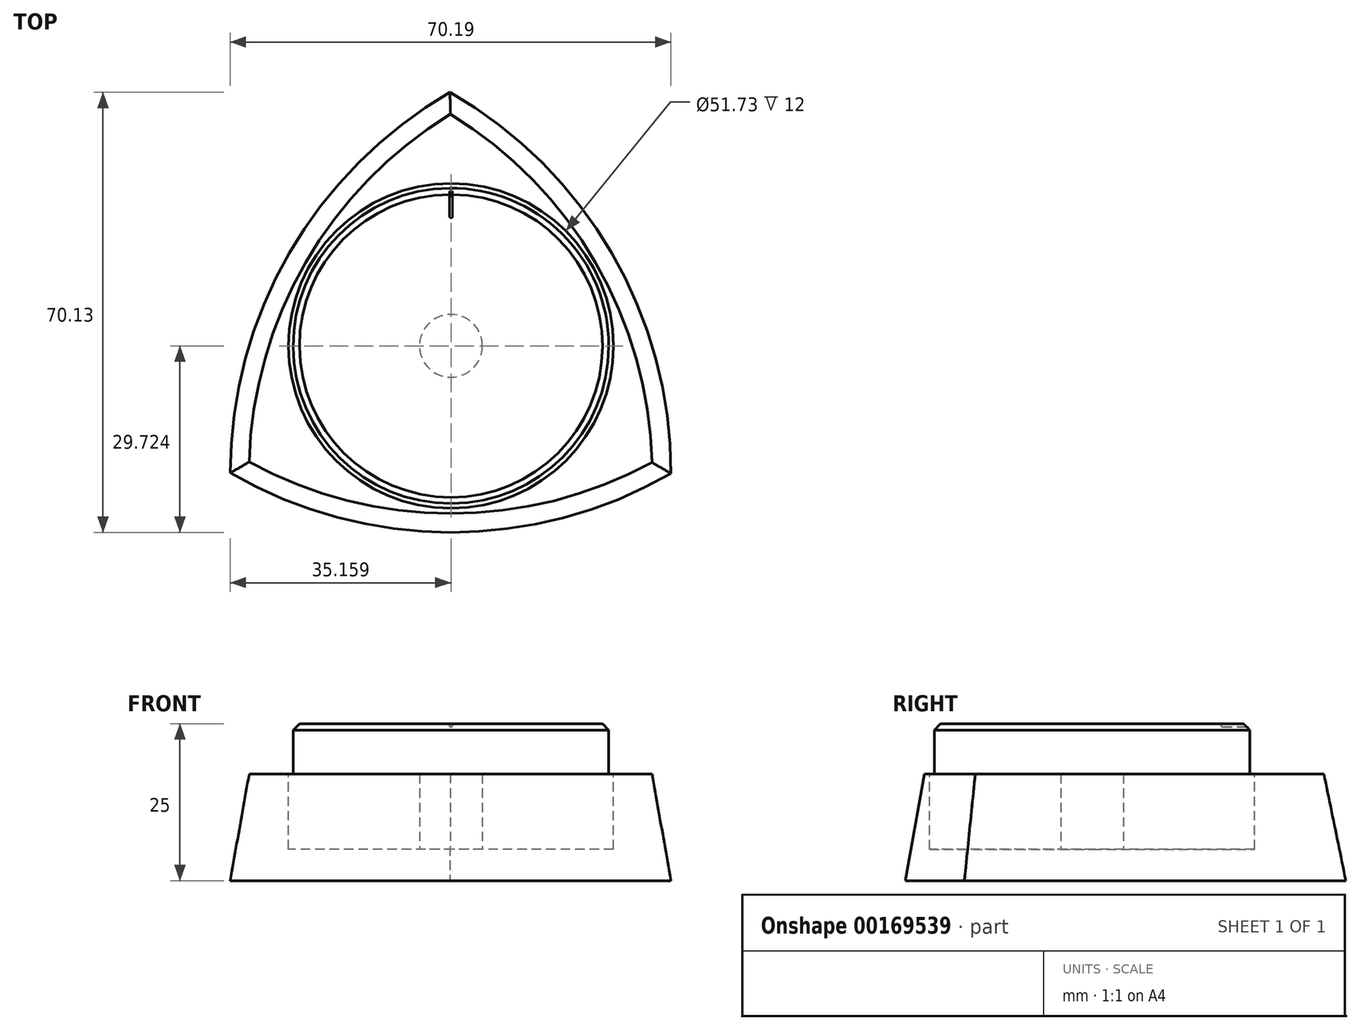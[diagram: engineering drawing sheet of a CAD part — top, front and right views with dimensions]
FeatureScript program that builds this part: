
annotation { "Feature Type Name" : "Feature", "Feature Type Description" : "" }
export const myFeature = defineFeature(function(context is Context, id is Id, definition is map)
    precondition{}
    {
        {
            var Q0;
            Q0=qCreatedBy(makeId("Top.planeOp"),FACE);
            var sketch = newSketch(context, id + "F0", { "sketchPlane" : qUnion([Q0])});
            skLineSegment(sketch, "E0", {"start": v(-35, 0) * mm, "end": v(35, 0) * mm});
            skLineSegment(sketch, "E1", {"start": v(35, 0) * mm, "end": v(0, 60.62) * mm});
            skLineSegment(sketch, "E2", {"start": v(0, 60.62) * mm, "end": v(-35, 0) * mm});
            skArc(sketch, "E3", {"start": v(35.02, -0.01) * mm, "mid": v(25.6, 35.08) * mm, "end": v(-0.15, 60.73) * mm});
            skArc(sketch, "E4", {"start": v(-0.15, 60.73) * mm, "mid": v(-25.77, 35.08) * mm, "end": v(-35.17, 0.07) * mm});
            skArc(sketch, "E5", {"start": v(-35.17, 0.07) * mm, "mid": v(-0.08, -9.4) * mm, "end": v(35.02, -0.01) * mm});
            skSolve(sketch);
        }
        {
            var Q0;
            Q0=makeQuery(id+"F0.imprint","IMPRINT",FACE,{"disambiguationData":[TD([[makeQuery(id+"F0.imprint","IMPRINT",EDGE,{"derivedFrom":sQuery(id+"F0.wireOp",EDGE,"E0")}),1.0]])]});
            var Q1;
            Q1=makeQuery(id+"F0.imprint","IMPRINT",FACE,{"disambiguationData":[TD([[makeQuery(id+"F0.imprint","IMPRINT",EDGE,{"derivedFrom":sQuery(id+"F0.wireOp",EDGE,"E0")}),-1.0]])]});
            extrude(context, id + "F1", {"entities" : qUnion([Q0, Q1]), "depth" : 17 * mm, "hasDraft" : true, "draftAngle" : 10 * degree, "draftPullDirection" : true});
        }
        {
            var Q0;
            Q0=makeQuery(id+"F1.opExtrude","CAP_FACE",FACE,{"disambiguationData":[OSD([sQuery(id+"F0.wireOp",EDGE,"E3"),sQuery(id+"F0.wireOp",EDGE,"E4"),sQuery(id+"F0.wireOp",EDGE,"E5")])],"isStart":false});
            var sketch = newSketch(context, id + "F2", { "sketchPlane" : qUnion([Q0])});
            skLineSegment(sketch, "E6", {"start": v(0.08, -6.4) * mm, "end": v(-0.14, 57.24) * mm, "construction": true});
            skPoint(sketch, "E6.startSnap0", {"position": v(-0.08, -6.4) * mm});
            skLineSegment(sketch, "E7", {"start": v(-23.17, 33.59) * mm, "end": v(32, 1.73) * mm, "construction": true});
            skLineSegment(sketch, "E8", {"start": v(23, 33.58) * mm, "end": v(-32.14, 1.81) * mm, "construction": true});
            skCircle(sketch, "E9", {"center": v(-0.01, 20.32) * mm, "radius": 25.87 * mm});
            skSolve(sketch);
        }
        {
            var Q0;
            Q0=makeQuery(id+"F2.imprint","IMPRINT",FACE,{"disambiguationData":[TD([[makeQuery(id+"F2.imprint","IMPRINT",EDGE,{"derivedFrom":sQuery(id+"F2.wireOp",EDGE,"E9")}),1.0]])]});
            extrude(context, id + "F3", {"entities" : qUnion([Q0]), "operationType" : NewBodyOperationType.REMOVE, "oppositeDirection" : true, "depth" : 12 * mm});
        }
        {
            var Q0;
            Q0=makeQuery(id+"F3.boolean.opBoolean","COPY",FACE,{"derivedFrom":makeQuery(id+"F3.opExtrude","CAP_FACE",FACE,{"disambiguationData":[OSD([sQuery(id+"F2.wireOp",EDGE,"E9")])],"isStart":false})});
            var sketch = newSketch(context, id + "F4", { "sketchPlane" : qUnion([Q0])});
            skCircle(sketch, "E10", {"center": v(-0.01, 20.32) * mm, "radius": 5 * mm});
            skCircle(sketch, "E11", {"center": v(-0.01, 20.32) * mm, "radius": 2.5 * mm});
            skSolve(sketch);
        }
        {
            var Q0;
            Q0=makeQuery(id+"F4.imprint","IMPRINT",FACE,{"disambiguationData":[TD([[makeQuery(id+"F4.imprint","IMPRINT",EDGE,{"derivedFrom":sQuery(id+"F4.wireOp",EDGE,"E10")}),1.0]])]});
            var Q1;
            Q1=makeQuery(id+"F1.opExtrude","CAP_FACE",FACE,{"disambiguationData":[OSD([sQuery(id+"F0.wireOp",EDGE,"E3"),sQuery(id+"F0.wireOp",EDGE,"E4"),sQuery(id+"F0.wireOp",EDGE,"E5")])],"isStart":false});
            extrude(context, id + "F5", {"entities" : qUnion([Q0]), "operationType" : NewBodyOperationType.ADD, "endBound" : BoundingType.UP_TO_SURFACE, "endBoundEntityFace" : qUnion([Q1]), "depth" : 25 * mm});
        }
        {
            var Q0;
            Q0=makeQuery(id+"F5.boolean.opBoolean","SPLIT",FACE,{"disambiguationData":[TD([makeQuery(id+"F5.opExtrude","SWEPT_FACE",FACE,{"disambiguationData":[OSD([sQuery(id+"F4.wireOp",EDGE,"E11")])]})])],"derivedFrom":makeQuery(id+"F3.boolean.opBoolean","COPY",FACE,{"derivedFrom":makeQuery(id+"F3.opExtrude","CAP_FACE",FACE,{"disambiguationData":[OSD([sQuery(id+"F2.wireOp",EDGE,"E9")])],"isStart":false})})});
            var Q1;
            Q1=makeQuery(id+"F5.opExtrude","CAP_FACE",FACE,{"disambiguationData":[OSD([sQuery(id+"F4.wireOp",EDGE,"E10"),sQuery(id+"F4.wireOp",EDGE,"E11")])],"isStart":false});
            extrude(context, id + "F6", {"entities" : qUnion([Q0]), "endBound" : BoundingType.UP_TO_SURFACE, "endBoundEntityFace" : qUnion([Q1]), "depth" : 10.5 * mm});
        }
        {
            var Q0;
            Q0=makeQuery(id+"F6.opExtrude","CAP_FACE",FACE,{"disambiguationData":[OSD([sQuery(id+"F2.wireOp",EDGE,"E9")])],"isStart":false});
            var sketch = newSketch(context, id + "F7", { "sketchPlane" : qUnion([Q0])});
            skCircle(sketch, "E12", {"center": v(-0.01, 20.32) * mm, "radius": 25.13 * mm});
            skSolve(sketch);
        }
        {
            var Q0;
            Q0 = qSketchRegion(id + "F7", true);
            extrude(context, id + "F8", {"entities" : qUnion([Q0]), "operationType" : NewBodyOperationType.ADD, "depth" : 8 * mm});
        }
        {
            var Q0;
            Q0=makeQuery(id+"F8.opExtrude","CAP_EDGE",EDGE,{"disambiguationData":[OSD([sQuery(id+"F7.wireOp",EDGE,"E12")])],"isStart":false});
            chamfer(context, id + "F9", {"entities" : qUnion([Q0]), "width" : 1 * mm, "tangentPropagation" : true});
        }
        {
            var Q0;
            Q0=makeQuery(id+"F8.opExtrude","CAP_FACE",FACE,{"disambiguationData":[OSD([sQuery(id+"F7.wireOp",EDGE,"E12")])],"isStart":false});
            var sketch = newSketch(context, id + "F10", { "sketchPlane" : qUnion([Q0])});
            skLineSegment(sketch, "E13", {"start": v(0, 45.8) * mm, "end": v(0, 40.8) * mm, "construction": true});
            skLineSegment(sketch, "E14", {"start": v(-0.15, 40.8) * mm, "end": v(0.15, 40.8) * mm});
            skLineSegment(sketch, "E15", {"start": v(0.15, 40.8) * mm, "end": v(0.15, 45.55) * mm});
            skLineSegment(sketch, "E16", {"start": v(0.15, 45.55) * mm, "end": v(-0.15, 45.55) * mm});
            skLineSegment(sketch, "E17", {"start": v(-0.15, 45.55) * mm, "end": v(-0.15, 40.8) * mm});
            skSolve(sketch);
        }
        {
            var Q0;
            {var subQ0=sQuery(id+"F10.wireOp",EDGE,"E16");Q0=makeQuery(id+"F10.imprint","IMPRINT",FACE,{"disambiguationData":[TD([[makeQuery(id+"F10.imprint","IMPRINT",EDGE,{"derivedFrom":subQ0}),1.0]])]});}
            var Q1;
            {var subQ0=sQuery(id+"F10.wireOp",EDGE,"E14");Q1=makeQuery(id+"F10.imprint","IMPRINT",FACE,{"disambiguationData":[TD([[makeQuery(id+"F10.imprint","IMPRINT",EDGE,{"derivedFrom":subQ0}),1.0]])]});}
            extrude(context, id + "F11", {"entities" : qUnion([Q0, Q1]), "operationType" : NewBodyOperationType.REMOVE, "oppositeDirection" : true, "depth" : 0.5 * mm});
        }
        {
            var Q0;
            Q0=makeQuery(id+"F11.boolean.opBoolean","COPY",EDGE,{"derivedFrom":makeQuery(id+"F11.opExtrude","CAP_EDGE",EDGE,{"disambiguationData":[OSD([sQuery(id+"F10.wireOp",EDGE,"E14")])],"isStart":false})});
            fillet(context, id + "F12", {"entities" : qUnion([Q0]), "radius" : 0.3 * mm, "tangentPropagation" : true, "allowEdgeOverflow" : false});
        }
        {
            var Q0;
            Q0=makeQuery(id+"F11.boolean.opBoolean","COPY",EDGE,{"derivedFrom":makeQuery(id+"F11.opExtrude","CAP_EDGE",EDGE,{"disambiguationData":[OSD([sQuery(id+"F10.wireOp",EDGE,"E17")])],"isStart":false})});
            var Q1;
            Q1=makeQuery(id+"F11.boolean.opBoolean","COPY",EDGE,{"derivedFrom":makeQuery(id+"F11.opExtrude","CAP_EDGE",EDGE,{"disambiguationData":[OSD([sQuery(id+"F10.wireOp",EDGE,"E15")])],"isStart":false})});
            fillet(context, id + "F13", {"entities" : qUnion([Q0, Q1]), "radius" : 0.1 * mm, "tangentPropagation" : true, "allowEdgeOverflow" : false});
        }
        {
            var Q0;
            Q0=makeQuery(id+"F11.boolean.opBoolean","COPY",EDGE,{"derivedFrom":makeQuery(id+"F11.opExtrude","CAP_EDGE",EDGE,{"disambiguationData":[OSD([sQuery(id+"F10.wireOp",EDGE,"E17")])],"isStart":true})});
            var Q1;
            Q1=makeQuery(id+"F13.opFillet","BLEND_EDGE",EDGE,{"blendedFrom":[makeQuery(id+"F11.boolean.opBoolean","COPY",EDGE,{"derivedFrom":makeQuery(id+"F11.opExtrude","SWEPT_EDGE",EDGE,{"disambiguationData":[OSD([sQuery(id+"F10.wireOp",EDGE,"E14"),sQuery(id+"F10.wireOp",EDGE,"E17")])]})}),makeQuery(id+"F8.opExtrude","CAP_FACE",FACE,{"disambiguationData":[OSD([sQuery(id+"F7.wireOp",EDGE,"E12")])],"isStart":false})],"blendedInto":[makeQuery(id+"F8.opExtrude","CAP_FACE",FACE,{"disambiguationData":[OSD([sQuery(id+"F7.wireOp",EDGE,"E12")])],"isStart":false})]});
            var Q2;
            Q2=makeQuery(id+"F11.boolean.opBoolean","COPY",EDGE,{"derivedFrom":makeQuery(id+"F11.opExtrude","CAP_EDGE",EDGE,{"disambiguationData":[OSD([sQuery(id+"F10.wireOp",EDGE,"E14")])],"isStart":true})});
            var Q3;
            Q3=makeQuery(id+"F13.opFillet","BLEND_EDGE",EDGE,{"blendedFrom":[makeQuery(id+"F11.boolean.opBoolean","COPY",EDGE,{"derivedFrom":makeQuery(id+"F11.opExtrude","SWEPT_EDGE",EDGE,{"disambiguationData":[OSD([sQuery(id+"F10.wireOp",EDGE,"E14"),sQuery(id+"F10.wireOp",EDGE,"E15")])]})}),makeQuery(id+"F8.opExtrude","CAP_FACE",FACE,{"disambiguationData":[OSD([sQuery(id+"F7.wireOp",EDGE,"E12")])],"isStart":false})],"blendedInto":[makeQuery(id+"F8.opExtrude","CAP_FACE",FACE,{"disambiguationData":[OSD([sQuery(id+"F7.wireOp",EDGE,"E12")])],"isStart":false})]});
            var Q4;
            Q4=makeQuery(id+"F11.boolean.opBoolean","COPY",EDGE,{"derivedFrom":makeQuery(id+"F11.opExtrude","CAP_EDGE",EDGE,{"disambiguationData":[OSD([sQuery(id+"F10.wireOp",EDGE,"E15")])],"isStart":true})});
            var Q5;
            Q5=makeQuery(id+"F11.boolean.opBoolean","INTERSECT",EDGE,{"derivedFrom":[makeQuery(id+"F9.opChamfer","BLEND_FACE",FACE,{"disambiguationData":[OSD([sQuery(id+"F7.wireOp",EDGE,"E12")])]}),makeQuery(id+"F11.opExtrude","SWEPT_FACE",FACE,{"disambiguationData":[OSD([sQuery(id+"F10.wireOp",EDGE,"E17")])]})]});
            var Q6;
            Q6=makeQuery(id+"F13.opFillet","BLEND_EDGE",EDGE,{"blendedFrom":[makeQuery(id+"F11.boolean.opBoolean","COPY",EDGE,{"derivedFrom":makeQuery(id+"F11.opExtrude","CAP_EDGE",EDGE,{"disambiguationData":[OSD([sQuery(id+"F10.wireOp",EDGE,"E17")])],"isStart":false})}),makeQuery(id+"F9.opChamfer","BLEND_FACE",FACE,{"disambiguationData":[OSD([sQuery(id+"F7.wireOp",EDGE,"E12")])]})],"blendedInto":[makeQuery(id+"F9.opChamfer","BLEND_FACE",FACE,{"disambiguationData":[OSD([sQuery(id+"F7.wireOp",EDGE,"E12")])]})]});
            var Q7;
            Q7=makeQuery(id+"F11.boolean.opBoolean","INTERSECT",EDGE,{"derivedFrom":[makeQuery(id+"F9.opChamfer","BLEND_FACE",FACE,{"disambiguationData":[OSD([sQuery(id+"F7.wireOp",EDGE,"E12")])]}),makeQuery(id+"F11.opExtrude","CAP_FACE",FACE,{"disambiguationData":[OSD([sQuery(id+"F10.wireOp",EDGE,"E14"),sQuery(id+"F10.wireOp",EDGE,"E15"),sQuery(id+"F10.wireOp",EDGE,"E16"),sQuery(id+"F10.wireOp",EDGE,"E17")])],"isStart":false})]});
            var Q8;
            Q8=makeQuery(id+"F13.opFillet","BLEND_EDGE",EDGE,{"blendedFrom":[makeQuery(id+"F11.boolean.opBoolean","COPY",EDGE,{"derivedFrom":makeQuery(id+"F11.opExtrude","CAP_EDGE",EDGE,{"disambiguationData":[OSD([sQuery(id+"F10.wireOp",EDGE,"E15")])],"isStart":false})}),makeQuery(id+"F9.opChamfer","BLEND_FACE",FACE,{"disambiguationData":[OSD([sQuery(id+"F7.wireOp",EDGE,"E12")])]})],"blendedInto":[makeQuery(id+"F9.opChamfer","BLEND_FACE",FACE,{"disambiguationData":[OSD([sQuery(id+"F7.wireOp",EDGE,"E12")])]})]});
            var Q9;
            Q9=makeQuery(id+"F11.boolean.opBoolean","INTERSECT",EDGE,{"derivedFrom":[makeQuery(id+"F9.opChamfer","BLEND_FACE",FACE,{"disambiguationData":[OSD([sQuery(id+"F7.wireOp",EDGE,"E12")])]}),makeQuery(id+"F11.opExtrude","SWEPT_FACE",FACE,{"disambiguationData":[OSD([sQuery(id+"F10.wireOp",EDGE,"E15")])]})]});
            chamfer(context, id + "F14", {"entities" : qUnion([Q0, Q1, Q2, Q3, Q4, Q5, Q6, Q7, Q8, Q9]), "width" : 0.07 * mm, "tangentPropagation" : true});
        }
    });
